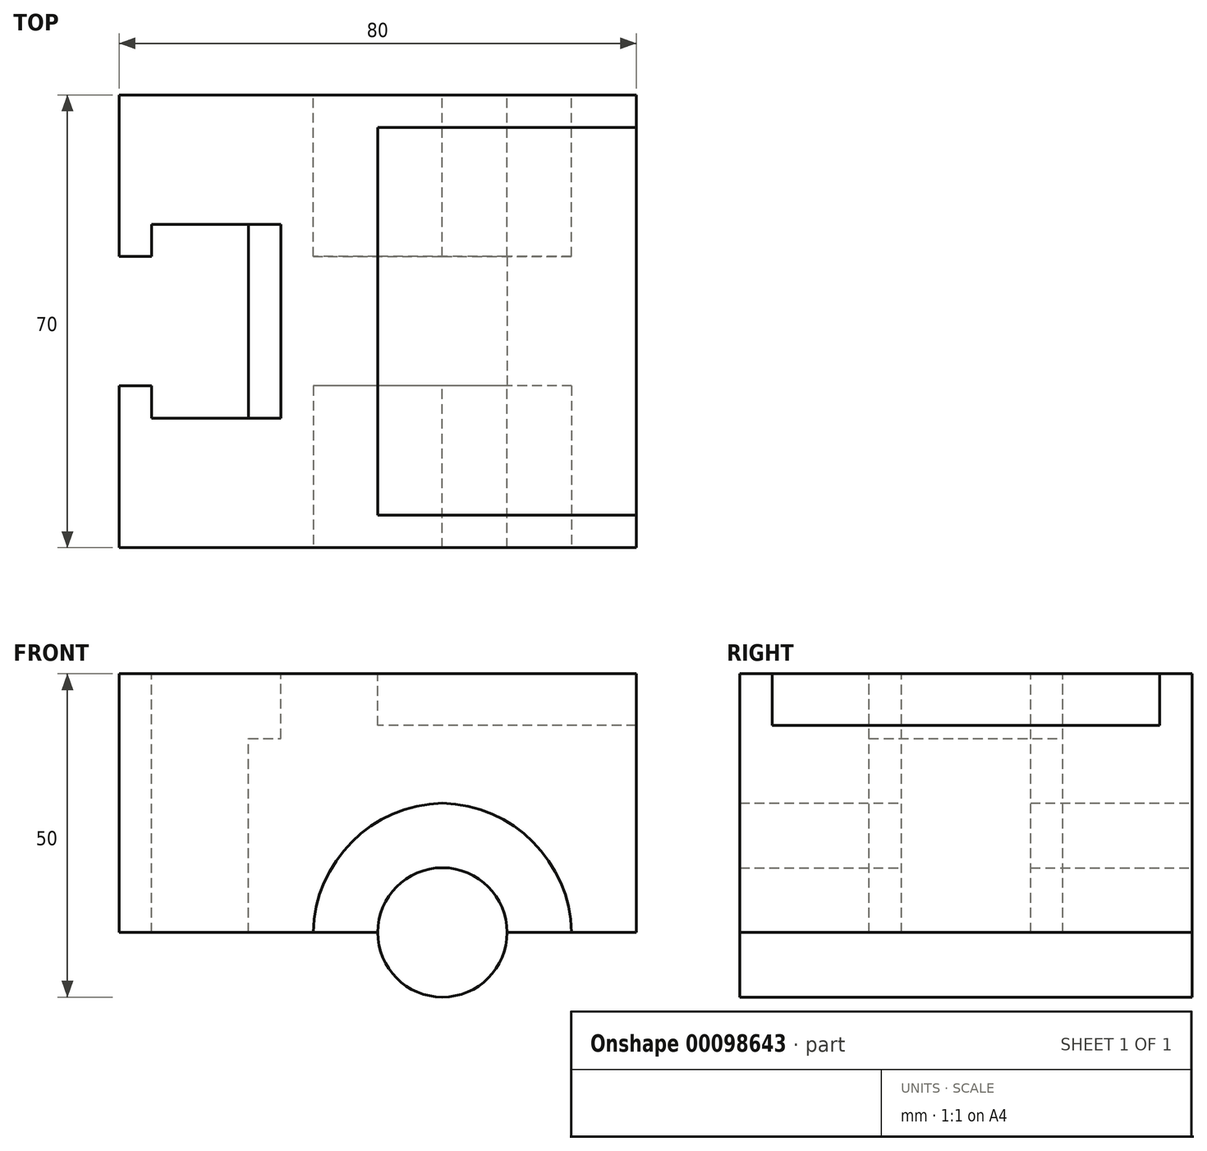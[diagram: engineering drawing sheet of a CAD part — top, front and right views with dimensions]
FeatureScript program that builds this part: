
annotation { "Feature Type Name" : "Feature", "Feature Type Description" : "" }
export const myFeature = defineFeature(function(context is Context, id is Id, definition is map)
    precondition{}
    {
        {
            var Q0;
            Q0=qCreatedBy(makeId("Right.planeOp"),FACE);
            var sketch = newSketch(context, id + "F0", { "sketchPlane" : qUnion([Q0])});
            skLineSegment(sketch, "E0.bottom", {"start": v(35, 20) * mm, "end": v(-35, 20) * mm});
            skLineSegment(sketch, "E0.top", {"start": v(35, -20) * mm, "end": v(-35, -20) * mm});
            skLineSegment(sketch, "E0.left", {"start": v(35, 20) * mm, "end": v(35, -20) * mm});
            skLineSegment(sketch, "E0.right", {"start": v(-35, 20) * mm, "end": v(-35, -20) * mm});
            skPoint(sketch, "E0.middle", {"position": v(0, 0) * mm});
            skSolve(sketch);
        }
        {
            var Q0;
            Q0=makeQuery(id+"F0.imprint","IMPRINT",FACE,{"disambiguationData":[TD([[makeQuery(id+"F0.imprint","IMPRINT",EDGE,{"derivedFrom":sQuery(id+"F0.wireOp",EDGE,"E0.bottom")}),1.0]])]});
            extrude(context, id + "F1", {"entities" : qUnion([Q0]), "depth" : 40 * mm, "hasSecondDirection" : true, "secondDirectionOppositeDirection" : true, "secondDirectionDepth" : 40 * mm});
        }
        {
            var Q0;
            Q0=makeQuery(id+"F1.opExtrude","SWEPT_FACE",FACE,{"disambiguationData":[OSD([sQuery(id+"F0.wireOp",EDGE,"E0.bottom")])]});
            var sketch = newSketch(context, id + "F2", { "sketchPlane" : qUnion([Q0])});
            skLineSegment(sketch, "E1.bottom", {"start": v(40, 0) * mm, "end": v(0, 0) * mm});
            skLineSegment(sketch, "E1.top", {"start": v(40, -30) * mm, "end": v(0, -30) * mm});
            skLineSegment(sketch, "E1.left", {"start": v(40, 0) * mm, "end": v(40, -30) * mm});
            skLineSegment(sketch, "E1.right", {"start": v(0, 0) * mm, "end": v(0, -30) * mm});
            skLineSegment(sketch, "E2.bottom", {"start": v(0, 0) * mm, "end": v(40, 0) * mm});
            skLineSegment(sketch, "E2.top", {"start": v(0, 30) * mm, "end": v(40, 30) * mm});
            skLineSegment(sketch, "E2.left", {"start": v(0, 0) * mm, "end": v(0, 30) * mm});
            skLineSegment(sketch, "E2.right", {"start": v(40, 0) * mm, "end": v(40, 30) * mm});
            skSolve(sketch);
        }
        {
            var Q0;
            Q0=makeQuery(id+"F2.imprint","IMPRINT",FACE,{"disambiguationData":[TD([[makeQuery(id+"F2.imprint","IMPRINT",EDGE,{"derivedFrom":sQuery(id+"F2.wireOp",EDGE,"E1.top")}),-1.0]])]});
            var Q1;
            Q1=makeQuery(id+"F2.imprint","IMPRINT",FACE,{"disambiguationData":[TD([[makeQuery(id+"F2.imprint","IMPRINT",EDGE,{"derivedFrom":sQuery(id+"F2.wireOp",EDGE,"E2.bottom")}),1.0]])]});
            extrude(context, id + "F3", {"entities" : qUnion([Q0, Q1]), "operationType" : NewBodyOperationType.REMOVE, "oppositeDirection" : true, "depth" : 8 * mm});
        }
        {
            var Q0;
            Q0=makeQuery(id+"F1.opExtrude","SWEPT_FACE",FACE,{"disambiguationData":[OSD([sQuery(id+"F0.wireOp",EDGE,"E0.bottom")])]});
            var sketch = newSketch(context, id + "F4", { "sketchPlane" : qUnion([Q0])});
            skLineSegment(sketch, "E3", {"start": v(-40, 0) * mm, "end": v(-20, 0) * mm});
            skLineSegment(sketch, "E4", {"start": v(-20, 0) * mm, "end": v(-20, 15) * mm});
            skLineSegment(sketch, "E5", {"start": v(-20, 15) * mm, "end": v(-35, 15) * mm});
            skLineSegment(sketch, "E6", {"start": v(-35, 15) * mm, "end": v(-35, 10) * mm});
            skLineSegment(sketch, "E7", {"start": v(-35, 10) * mm, "end": v(-40, 10) * mm});
            skLineSegment(sketch, "E8", {"start": v(-40, 10) * mm, "end": v(-40, 0) * mm});
            skLineSegment(sketch, "E9.MirrorCS", {"start": v(-35, -10) * mm, "end": v(-40, -10) * mm});
            skLineSegment(sketch, "E10.MirrorCS", {"start": v(-35, -15) * mm, "end": v(-35, -10) * mm});
            skLineSegment(sketch, "E11.MirrorCS", {"start": v(-40, -10) * mm, "end": v(-40, 0) * mm});
            skLineSegment(sketch, "E12.MirrorCS", {"start": v(-20, -15) * mm, "end": v(-35, -15) * mm});
            skLineSegment(sketch, "E13.MirrorCS", {"start": v(-20, 0) * mm, "end": v(-20, -15) * mm});
            skSolve(sketch);
        }
        {
            var Q0;
            Q0=makeQuery(id+"F4.imprint","IMPRINT",FACE,{"disambiguationData":[TD([[makeQuery(id+"F4.imprint","IMPRINT",EDGE,{"derivedFrom":sQuery(id+"F4.wireOp",EDGE,"E3")}),1.0]])]});
            var Q1;
            Q1=makeQuery(id+"F4.imprint","IMPRINT",FACE,{"disambiguationData":[TD([[makeQuery(id+"F4.imprint","IMPRINT",EDGE,{"derivedFrom":sQuery(id+"F4.wireOp",EDGE,"E3")}),-1.0]])]});
            extrude(context, id + "F5", {"entities" : qUnion([Q0, Q1]), "operationType" : NewBodyOperationType.REMOVE, "oppositeDirection" : true, "depth" : 40 * mm});
        }
        {
            var Q0;
            Q0=makeQuery(id+"F1.opExtrude","SWEPT_FACE",FACE,{"disambiguationData":[OSD([sQuery(id+"F0.wireOp",EDGE,"E0.right")])]});
            var sketch = newSketch(context, id + "F6", { "sketchPlane" : qUnion([Q0])});
            skLineSegment(sketch, "E14.bottom", {"start": v(-10, -20) * mm, "end": v(30, -20) * mm});
            skLineSegment(sketch, "E14.top", {"start": v(-10, 0) * mm, "end": v(30, 0) * mm});
            skLineSegment(sketch, "E14.left", {"start": v(-10, -20) * mm, "end": v(-10, 0) * mm});
            skLineSegment(sketch, "E14.right", {"start": v(30, -20) * mm, "end": v(30, 0) * mm});
            skSolve(sketch);
        }
        {
            var Q0;
            Q0=makeQuery(id+"F6.imprint","IMPRINT",FACE,{"disambiguationData":[TD([[makeQuery(id+"F6.imprint","IMPRINT",EDGE,{"derivedFrom":sQuery(id+"F6.wireOp",EDGE,"E14.bottom")}),-1.0]])]});
            extrude(context, id + "F7", {"entities" : qUnion([Q0]), "operationType" : NewBodyOperationType.REMOVE, "oppositeDirection" : true, "depth" : 25 * mm});
        }
        {
            var Q0;
            Q0=makeQuery(id+"F7.boolean.opBoolean","COPY",FACE,{"derivedFrom":makeQuery(id+"F7.opExtrude","CAP_FACE",FACE,{"disambiguationData":[OSD([sQuery(id+"F6.wireOp",EDGE,"E14.bottom"),sQuery(id+"F6.wireOp",EDGE,"E14.top"),sQuery(id+"F6.wireOp",EDGE,"E14.left"),sQuery(id+"F6.wireOp",EDGE,"E14.right")])],"isStart":false})});
            var sketch = newSketch(context, id + "F8", { "sketchPlane" : qUnion([Q0])});
            skCircle(sketch, "E15", {"center": v(10, -20) * mm, "radius": 10 * mm});
            skSolve(sketch);
        }
        {
            var Q0;
            {var subQ0=sQuery(id+"F8.wireOp",EDGE,"E15");var subQ1=makeQuery(id+"F7.boolean.opBoolean","COPY",EDGE,{"derivedFrom":makeQuery(id+"F7.opExtrude","CAP_EDGE",EDGE,{"disambiguationData":[OSD([sQuery(id+"F6.wireOp",EDGE,"E14.bottom")])],"isStart":false})});var subQ2=makeQuery(id+"F8.imprint","INTERSECT",VERTEX,{"disambiguationData":[OD(0.0)],"derivedFrom":[subQ1,subQ0]});Q0=makeQuery(id+"F8.imprint","IMPRINT",FACE,{"disambiguationData":[TD([[makeQuery(id+"F8.imprint","IMPRINT",EDGE,{"disambiguationData":[TD([[subQ2,1.0]])],"derivedFrom":subQ0}),1.0]])]});}
            var Q1;
            {var subQ0=sQuery(id+"F8.wireOp",EDGE,"E15");var subQ1=makeQuery(id+"F7.boolean.opBoolean","COPY",EDGE,{"derivedFrom":makeQuery(id+"F7.opExtrude","CAP_EDGE",EDGE,{"disambiguationData":[OSD([sQuery(id+"F6.wireOp",EDGE,"E14.bottom")])],"isStart":false})});var subQ2=makeQuery(id+"F8.imprint","INTERSECT",VERTEX,{"disambiguationData":[OD(0.0)],"derivedFrom":[subQ1,subQ0]});Q1=makeQuery(id+"F8.imprint","IMPRINT",FACE,{"disambiguationData":[TD([[makeQuery(id+"F8.imprint","IMPRINT",EDGE,{"disambiguationData":[TD([[subQ2,-1.0]])],"derivedFrom":subQ0}),1.0]])]});}
            extrude(context, id + "F9", {"entities" : qUnion([Q0, Q1]), "operationType" : NewBodyOperationType.ADD, "depth" : 25 * mm});
        }
        {
            var Q0;
            Q0=makeQuery(id+"F1.opExtrude","SWEPT_FACE",FACE,{"disambiguationData":[OSD([sQuery(id+"F0.wireOp",EDGE,"E0.left")])]});
            var sketch = newSketch(context, id + "F10", { "sketchPlane" : qUnion([Q0])});
            skLineSegment(sketch, "E16.bottom", {"start": v(40, 20) * mm, "end": v(-40, 20) * mm});
            skLineSegment(sketch, "E16.top", {"start": v(40, -20) * mm, "end": v(-40, -20) * mm});
            skLineSegment(sketch, "E16.left", {"start": v(40, 20) * mm, "end": v(40, -20) * mm});
            skLineSegment(sketch, "E16.right", {"start": v(-40, 20) * mm, "end": v(-40, -20) * mm});
            skSolve(sketch);
        }
        {
            var Q0;
            Q0=makeQuery(id+"F10.imprint","IMPRINT",FACE,{"disambiguationData":[TD([[makeQuery(id+"F10.imprint","IMPRINT",EDGE,{"derivedFrom":sQuery(id+"F10.wireOp",EDGE,"E16.bottom")}),-1.0]])]});
            extrude(context, id + "F11", {"entities" : qUnion([Q0]), "operationType" : NewBodyOperationType.REMOVE, "oppositeDirection" : true, "depth" : 35 * mm});
        }
        {
            var Q0;
            Q0=makeQuery(id+"F1.opExtrude","SWEPT_BODY",BODY,{"disambiguationData":[OSD([sQuery(id+"F0.wireOp",EDGE,"E0.bottom"),sQuery(id+"F0.wireOp",EDGE,"E0.top"),sQuery(id+"F0.wireOp",EDGE,"E0.left"),sQuery(id+"F0.wireOp",EDGE,"E0.right")])]});
            var Q1;
            Q1=qCreatedBy(makeId("Front.planeOp"),FACE);
            mirror(context, id + "F12", {"operationType" : NewBodyOperationType.ADD, "entities" : qUnion([Q0]), "mirrorPlane" : qUnion([Q1])});
        }
        {
            var Q0;
            Q0=makeQuery(id+"F9.opExtrude","CAP_FACE",FACE,{"disambiguationData":[OSD([sQuery(id+"F8.wireOp",EDGE,"E15")])],"isStart":true});
            extrude(context, id + "F13", {"entities" : qUnion([Q0]), "operationType" : NewBodyOperationType.ADD, "depth" : 25 * mm});
        }
        {
            var Q0;
            Q0=makeQuery(id+"F12.opPattern","COPY",EDGE,{"derivedFrom":makeQuery(id+"F7.boolean.opBoolean","COPY",EDGE,{"derivedFrom":makeQuery(id+"F7.opExtrude","SWEPT_EDGE",EDGE,{"disambiguationData":[OSD([sQuery(id+"F6.wireOp",EDGE,"E14.top"),sQuery(id+"F6.wireOp",EDGE,"E14.right")])]})}),"instanceName":"1"});
            var Q1;
            Q1=makeQuery(id+"F12.opPattern","COPY",EDGE,{"derivedFrom":makeQuery(id+"F7.boolean.opBoolean","COPY",EDGE,{"derivedFrom":makeQuery(id+"F7.opExtrude","SWEPT_EDGE",EDGE,{"disambiguationData":[OSD([sQuery(id+"F6.wireOp",EDGE,"E14.top"),sQuery(id+"F6.wireOp",EDGE,"E14.left")])]})}),"instanceName":"1"});
            var Q2;
            Q2=makeQuery(id+"F7.boolean.opBoolean","COPY",EDGE,{"derivedFrom":makeQuery(id+"F7.opExtrude","SWEPT_EDGE",EDGE,{"disambiguationData":[OSD([sQuery(id+"F6.wireOp",EDGE,"E14.top"),sQuery(id+"F6.wireOp",EDGE,"E14.right")])]})});
            var Q3;
            Q3=makeQuery(id+"F7.boolean.opBoolean","COPY",EDGE,{"derivedFrom":makeQuery(id+"F7.opExtrude","SWEPT_EDGE",EDGE,{"disambiguationData":[OSD([sQuery(id+"F6.wireOp",EDGE,"E14.top"),sQuery(id+"F6.wireOp",EDGE,"E14.left")])]})});
            fillet(context, id + "F14", {"entities" : qUnion([Q0, Q1, Q2, Q3]), "radius" : 20.5 * mm, "tangentPropagation" : true, "allowEdgeOverflow" : false});
        }
        {
            var Q0;
            {var subQ0=makeQuery(id+"F1.opExtrude","SWEPT_FACE",FACE,{"disambiguationData":[OSD([sQuery(id+"F0.wireOp",EDGE,"E0.bottom")])]});Q0=makeQuery(id+"F12.boolean.opBoolean","MERGE",FACE,{"derivedFrom":[subQ0,makeQuery(id+"F12.opPattern","COPY",FACE,{"derivedFrom":subQ0,"instanceName":"1"})]});}
            var sketch = newSketch(context, id + "F15", { "sketchPlane" : qUnion([Q0])});
            skLineSegment(sketch, "E17.bottom", {"start": v(-20, 15) * mm, "end": v(-15, 15) * mm});
            skLineSegment(sketch, "E17.top", {"start": v(-20, -15) * mm, "end": v(-15, -15) * mm});
            skLineSegment(sketch, "E17.left", {"start": v(-20, 15) * mm, "end": v(-20, -15) * mm});
            skLineSegment(sketch, "E17.right", {"start": v(-15, 15) * mm, "end": v(-15, -15) * mm});
            skSolve(sketch);
        }
        {
            var Q0;
            Q0=makeQuery(id+"F15.imprint","IMPRINT",FACE,{"disambiguationData":[TD([[makeQuery(id+"F15.imprint","IMPRINT",EDGE,{"derivedFrom":sQuery(id+"F15.wireOp",EDGE,"E17.bottom")}),-1.0]])]});
            extrude(context, id + "F16", {"entities" : qUnion([Q0]), "operationType" : NewBodyOperationType.REMOVE, "oppositeDirection" : true, "depth" : 10 * mm});
        }
    });
